# Revit family: Wing W100EC_wall
name_source: partatom
category: Mechanical Equipment
revit_build: Autodesk Revit 2017 (Build: 20170118_1100(x64)
units: mm (PartAtom-declared; Revit-internal decimal feet)

## family parameters
Cut with Voids When Loaded = No
Host = Face
OmniClass Number = 23.75.70.21.17
OmniClass Title = Air Curtains
Part Type = Normal
Room Calculation Point = No
Round Connector Dimension = Use Diameter
Shared = No

## types (3) — shared parameters
Connection stub pipe diameter inlet = 1"
Connection stub pipe diameter outlet = 1"
Default Elevation = 1 m
Device inlet air temperature = 5 °C
Device inlet water temperature = 70 °C
Device outlet water temperature = 50 °C
Electrical Potential = 230 V
Frequency = 50 Hz
Manufacturer = VTS
Model = WING W100EC
Motor rated current EC = 1 A
Protection rating EC = 20
URL = http://vtsgroup.com
W = 1 m
Weight = 27.00 kg
zero-valued in all types: a

## per-type parameters (varying)
| type | Device heating power | Device outlet air temperature | FAN speed | Fan output | Horizontal range | Medium flow | Vertical range |
| WING W100EC HIGH | 12 kW | 23 °C | HIGH | 1850.0 m³/h | 4 m | 0.5 m³/h | 4 m |
| WING W100EC MEDIUM | 10 kW | 24 °C | MEDIUM | 1350.0 m³/h | 3 m | 0.4 m³/h | 3 m |
| WING W100EC LOW | 8 kW | 27 °C | LOW | 880.0 m³/h | 2 m | 0.3 m³/h | 2 m |

## geometry (parser evidence)
native form markers: Blend x2, Sweep x9
no freeform markers — native parametric forms only
